# Revit family: Pannello Fotovoltaico
name_source: partatom
category: Attrezzature speciali
revit_build: Autodesk Revit Architecture 2012 (Build: 20110309_2315)
units: mm (PartAtom-declared; Revit-internal decimal feet)

## types (3) — shared parameters
Prospetto di default = 1219 mm
c_materiale = vetro fotovoltaico
zero-valued in all types: c_costopannello

## per-type parameters (varying)
| type | c_areapannello | c_larghezzapannello | c_lunghezzapannello | c_pesopannello | c_potenza | c_spessorepannello |
| Sunerg 225Wp 1645x992x46 | 1.63 m² | 992 mm  [stored 3.25459 ft] | 1645 mm | 22 | 225 | 46 mm  [stored 0.150919 ft] |
| Trina 225Wp 1650x992x46 | 1.64 m² | 992 mm  [stored 3.25459 ft] | 1650 mm  [stored 5.41339 ft] | 19.5 | 225 | 46 mm  [stored 0.150919 ft] |
| Wurth 80Wp 1250x605x35 | 0.76 m² | 605 mm  [stored 1.98491 ft] | 1250 mm  [stored 4.10105 ft] | 12.71 | 80 | 35 mm  [stored 0.114829 ft] |

note: [stored X ft] marks values corroborated as IEEE doubles in the binary element streams (Revit-internal decimal feet)
